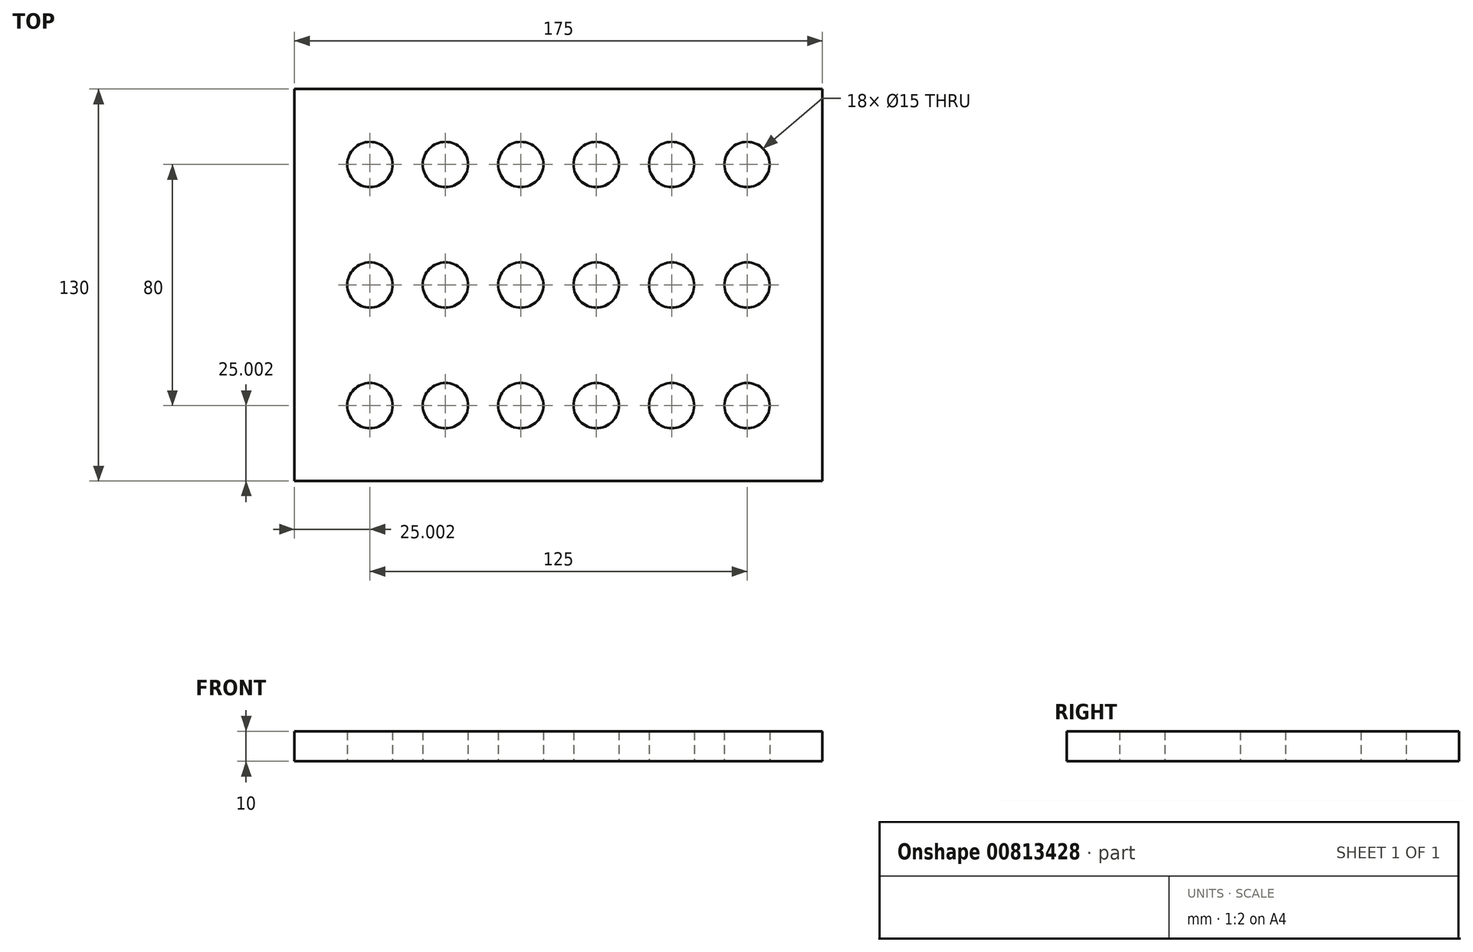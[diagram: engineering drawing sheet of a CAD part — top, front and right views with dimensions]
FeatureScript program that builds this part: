
annotation { "Feature Type Name" : "Feature", "Feature Type Description" : "" }
export const myFeature = defineFeature(function(context is Context, id is Id, definition is map)
    precondition{}
    {
        {
            var Q0;
            Q0=qCreatedBy(makeId("Top.planeOp"),FACE);
            var sketch = newSketch(context, id + "F0", { "sketchPlane" : qUnion([Q0])});
            skLineSegment(sketch, "E0.bottom", {"start": v(-64.49, 51.3) * mm, "end": v(110.51, 51.3) * mm});
            skLineSegment(sketch, "E0.top", {"start": v(-64.49, -78.7) * mm, "end": v(110.51, -78.7) * mm});
            skLineSegment(sketch, "E0.left", {"start": v(-64.49, 51.3) * mm, "end": v(-64.49, -78.7) * mm});
            skLineSegment(sketch, "E0.right", {"start": v(110.51, 51.3) * mm, "end": v(110.51, -78.7) * mm});
            skCircle(sketch, "E1", {"center": v(-39.49, 26.3) * mm, "radius": 7.5 * mm});
            skCircle(sketch, "E2.0.1.0", {"center": v(-39.49, -13.7) * mm, "radius": 7.5 * mm});
            skCircle(sketch, "E2.0.2.0", {"center": v(-39.49, -53.7) * mm, "radius": 7.5 * mm});
            skCircle(sketch, "E2.1.0.0", {"center": v(-14.49, 26.3) * mm, "radius": 7.5 * mm});
            skCircle(sketch, "E2.1.1.0", {"center": v(-14.49, -13.7) * mm, "radius": 7.5 * mm});
            skCircle(sketch, "E2.1.2.0", {"center": v(-14.49, -53.7) * mm, "radius": 7.5 * mm});
            skCircle(sketch, "E2.2.0.0", {"center": v(10.51, 26.3) * mm, "radius": 7.5 * mm});
            skCircle(sketch, "E2.2.1.0", {"center": v(10.51, -13.7) * mm, "radius": 7.5 * mm});
            skCircle(sketch, "E2.2.2.0", {"center": v(10.51, -53.7) * mm, "radius": 7.5 * mm});
            skCircle(sketch, "E2.3.0.0", {"center": v(35.51, 26.3) * mm, "radius": 7.5 * mm});
            skCircle(sketch, "E2.3.1.0", {"center": v(35.51, -13.7) * mm, "radius": 7.5 * mm});
            skCircle(sketch, "E2.3.2.0", {"center": v(35.51, -53.7) * mm, "radius": 7.5 * mm});
            skCircle(sketch, "E2.4.0.0", {"center": v(60.51, 26.3) * mm, "radius": 7.5 * mm});
            skCircle(sketch, "E2.4.1.0", {"center": v(60.51, -13.7) * mm, "radius": 7.5 * mm});
            skCircle(sketch, "E2.4.2.0", {"center": v(60.51, -53.7) * mm, "radius": 7.5 * mm});
            skCircle(sketch, "E2.5.0.0", {"center": v(85.51, 26.3) * mm, "radius": 7.5 * mm});
            skCircle(sketch, "E2.5.1.0", {"center": v(85.51, -13.7) * mm, "radius": 7.5 * mm});
            skCircle(sketch, "E2.5.2.0", {"center": v(85.51, -53.7) * mm, "radius": 7.5 * mm});
            skLineSegment(sketch, "E2.direction1", {"start": v(-39.49, 26.3) * mm, "end": v(-14.49, 26.3) * mm, "construction": true});
            skLineSegment(sketch, "E2.direction2", {"start": v(-39.49, 26.3) * mm, "end": v(-39.49, -13.7) * mm, "construction": true});
            skSolve(sketch);
        }
        {
            var Q0;
            Q0 = qSketchRegion(id + "F0", true);
            extrude(context, id + "F1", {"entities" : qUnion([Q0]), "depth" : 10 * mm, "offsetDistance" : 25.4 * mm});
        }
    });
